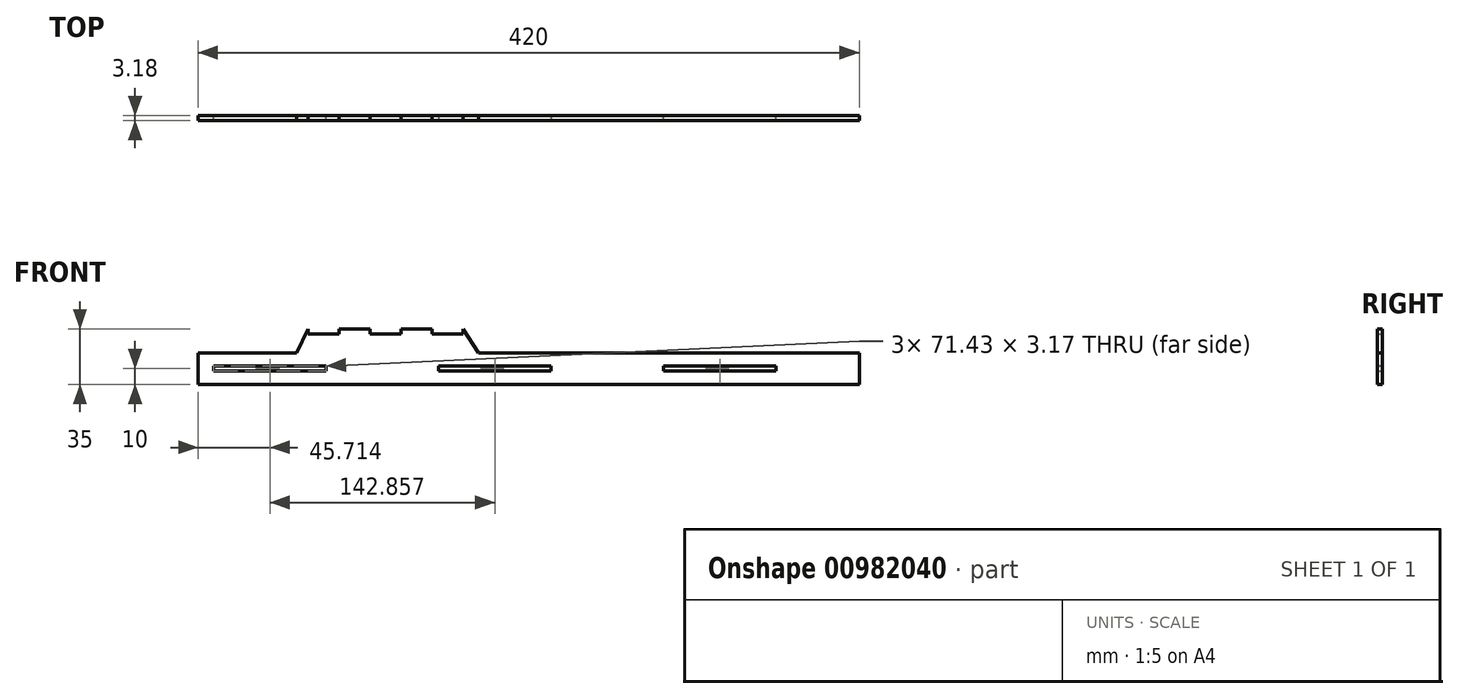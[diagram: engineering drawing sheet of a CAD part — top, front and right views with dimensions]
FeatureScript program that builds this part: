
annotation { "Feature Type Name" : "Feature", "Feature Type Description" : "" }
export const myFeature = defineFeature(function(context is Context, id is Id, definition is map)
    precondition{}
    {
        {
            var Q0;
            Q0=qCreatedBy(makeId("Front.planeOp"),FACE);
            var sketch = newSketch(context, id + "F0", { "sketchPlane" : qUnion([Q0])});
            skLineSegment(sketch, "E0.right", {"start": v(-260, -10) * mm, "end": v(-260, 10) * mm});
            skPoint(sketch, "E0.middle", {"position": v(0, 0) * mm});
            skLineSegment(sketch, "E1.bottom", {"start": v(35.71, -1.59) * mm, "end": v(-35.71, -1.59) * mm, "construction": true});
            skLineSegment(sketch, "E1.top", {"start": v(35.71, 1.59) * mm, "end": v(-35.71, 1.59) * mm, "construction": true});
            skLineSegment(sketch, "E1.left", {"start": v(35.71, -1.59) * mm, "end": v(35.71, 1.59) * mm, "construction": true});
            skLineSegment(sketch, "E1.right", {"start": v(-35.71, -1.59) * mm, "end": v(-35.71, 1.59) * mm});
            skLineSegment(sketch, "E2.1.0.0", {"start": v(107.14, 1.59) * mm, "end": v(35.71, 1.59) * mm});
            skLineSegment(sketch, "E2.1.0.1", {"start": v(107.14, -1.59) * mm, "end": v(35.71, -1.59) * mm});
            skLineSegment(sketch, "E2.1.0.2", {"start": v(107.14, -1.59) * mm, "end": v(107.14, 1.59) * mm});
            skLineSegment(sketch, "E2.1.0.3", {"start": v(35.71, -1.59) * mm, "end": v(35.71, 1.59) * mm});
            skLineSegment(sketch, "E2.2.0.0", {"start": v(178.57, 1.59) * mm, "end": v(107.14, 1.59) * mm, "construction": true});
            skLineSegment(sketch, "E2.2.0.1", {"start": v(178.57, -1.59) * mm, "end": v(107.14, -1.59) * mm, "construction": true});
            skLineSegment(sketch, "E2.2.0.3", {"start": v(107.14, -1.59) * mm, "end": v(107.14, 1.59) * mm, "construction": true});
            skLineSegment(sketch, "E2.direction1", {"start": v(-35.71, -1.59) * mm, "end": v(35.71, -1.59) * mm, "construction": true});
            skLineSegment(sketch, "E3.MirrorCS", {"start": v(-250, -1.59) * mm, "end": v(-250, 1.59) * mm});
            skLineSegment(sketch, "E4.MirrorCS", {"start": v(-178.57, -1.59) * mm, "end": v(-178.57, 1.59) * mm});
            skLineSegment(sketch, "E5.MirrorCS", {"start": v(-250, -1.59) * mm, "end": v(-178.57, -1.59) * mm});
            skLineSegment(sketch, "E6.MirrorCS", {"start": v(-250, 1.59) * mm, "end": v(-178.57, 1.59) * mm});
            skLineSegment(sketch, "E7.MirrorCS", {"start": v(-107.14, -1.59) * mm, "end": v(-107.14, 1.59) * mm});
            skLineSegment(sketch, "E8.MirrorCS", {"start": v(-35.71, -1.59) * mm, "end": v(-35.71, 1.59) * mm, "construction": true});
            skLineSegment(sketch, "E9.MirrorCS", {"start": v(-107.14, 1.59) * mm, "end": v(-35.71, 1.59) * mm});
            skLineSegment(sketch, "E10.MirrorCS", {"start": v(-107.14, -1.59) * mm, "end": v(-35.71, -1.59) * mm});
            skLineSegment(sketch, "E11.bottom", {"start": v(-250, -5.81) * mm, "end": v(150, -5.81) * mm, "construction": true});
            skLineSegment(sketch, "E12", {"start": v(-35.71, 1.59) * mm, "end": v(-35.71, 33.6) * mm, "construction": true});
            skLineSegment(sketch, "E13", {"start": v(-190, 25) * mm, "end": v(-190, 10) * mm});
            skLineSegment(sketch, "E14", {"start": v(-91.58, 25) * mm, "end": v(-91.58, 10) * mm});
            skLineSegment(sketch, "E15", {"start": v(-170.32, 25) * mm, "end": v(-170.32, 21.83) * mm});
            skLineSegment(sketch, "E16", {"start": v(-150.63, 21.83) * mm, "end": v(-150.63, 25) * mm});
            skLineSegment(sketch, "E17", {"start": v(-130.95, 25) * mm, "end": v(-130.95, 21.83) * mm});
            skLineSegment(sketch, "E18", {"start": v(-111.26, 21.83) * mm, "end": v(-111.26, 25) * mm});
            skLineSegment(sketch, "E19", {"start": v(-190, 25) * mm, "end": v(-197.49, 10) * mm});
            skLineSegment(sketch, "E20", {"start": v(-150.63, 23.41) * mm, "end": v(-130.95, 23.41) * mm, "construction": true});
            skLineSegment(sketch, "E21.MirrorCS", {"start": v(-130.95, 21.83) * mm, "end": v(-130.95, 25) * mm});
            skLineSegment(sketch, "E22.MirrorCS", {"start": v(-150.63, 25) * mm, "end": v(-150.63, 21.83) * mm});
            skLineSegment(sketch, "E23.MirrorCS", {"start": v(-111.26, 21.83) * mm, "end": v(-91.58, 21.82) * mm});
            skLineSegment(sketch, "E24.MirrorCS", {"start": v(-190, 21.82) * mm, "end": v(-170.32, 21.82) * mm});
            skLineSegment(sketch, "E25.MirrorCS", {"start": v(-150.63, 21.83) * mm, "end": v(-130.95, 21.83) * mm});
            skLineSegment(sketch, "E26.MirrorCS", {"start": v(-170.32, 25) * mm, "end": v(-150.63, 25) * mm});
            skLineSegment(sketch, "E27.MirrorCS", {"start": v(-111.26, 25) * mm, "end": v(-111.26, 21.83) * mm});
            skLineSegment(sketch, "E28.MirrorCS", {"start": v(-130.95, 25) * mm, "end": v(-111.26, 25) * mm});
            skLineSegment(sketch, "E29.MirrorCS", {"start": v(-170.32, 21.82) * mm, "end": v(-170.32, 25) * mm});
            skLineSegment(sketch, "E30", {"start": v(-190, 25) * mm, "end": v(-91.58, 25) * mm, "construction": true});
            skLineSegment(sketch, "E31", {"start": v(-91.58, 25) * mm, "end": v(-81.9, 10) * mm});
            skLineSegment(sketch, "E32", {"start": v(150, -5.81) * mm, "end": v(150, 10) * mm, "construction": true});
            skLineSegment(sketch, "E33", {"start": v(160, 10) * mm, "end": v(160, -10) * mm});
            skLineSegment(sketch, "E34", {"start": v(-260, -10) * mm, "end": v(160, -10) * mm});
            skLineSegment(sketch, "E35", {"start": v(-260, 10) * mm, "end": v(160, 10) * mm});
            skSolve(sketch);
        }
        {
            var Q0;
            Q0 = qSketchRegion(id + "F0", true);
            extrude(context, id + "F1", {"entities" : qUnion([Q0]), "depth" : 3.17 * mm, "offsetDistance" : 25 * mm});
        }
    });
